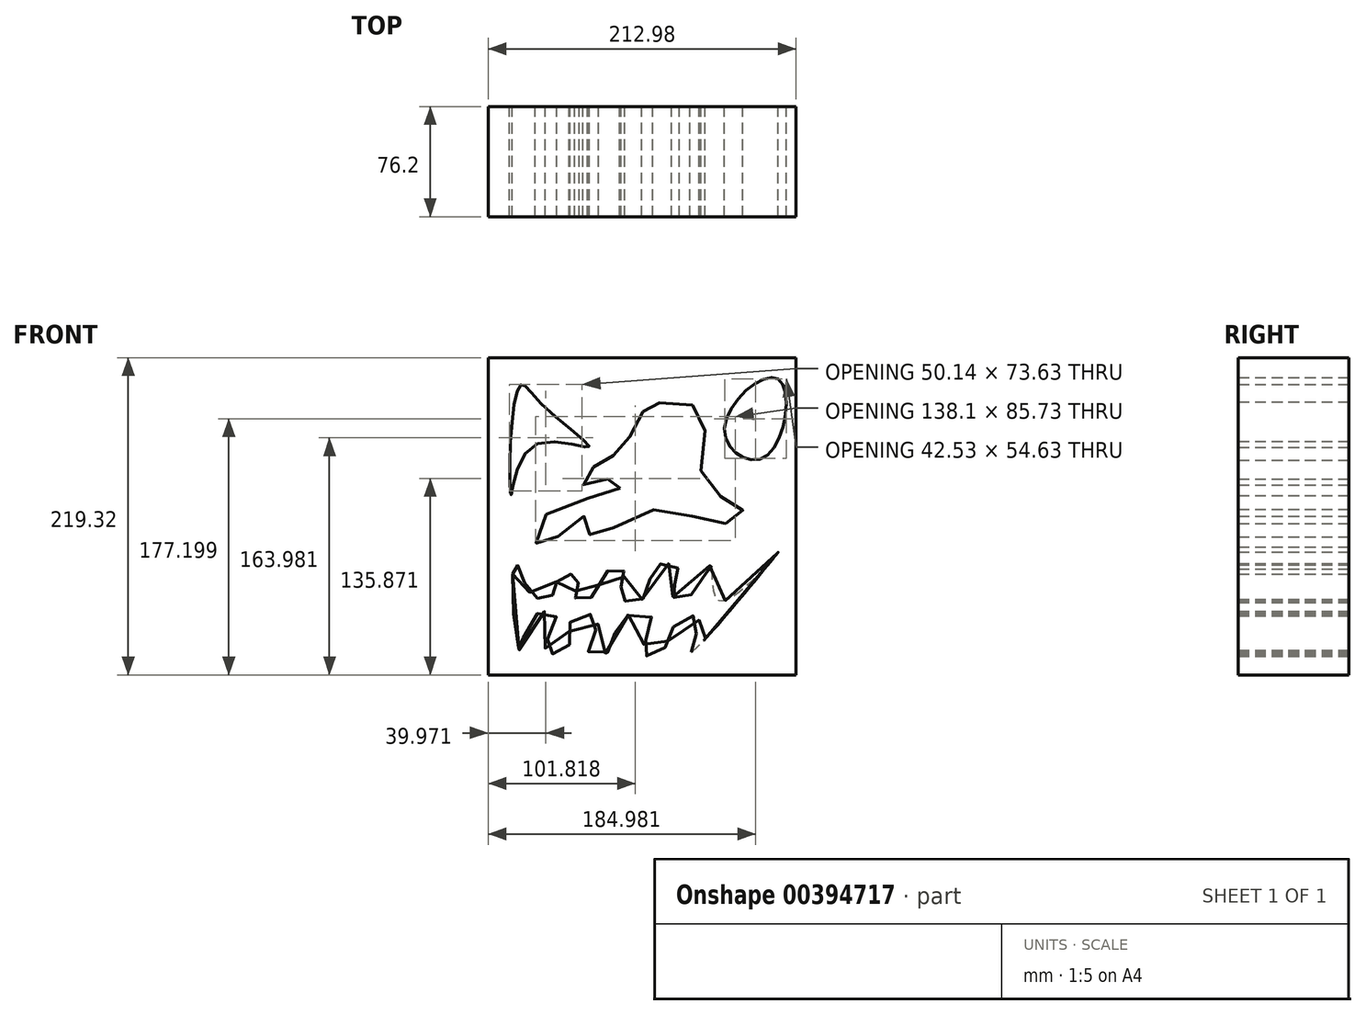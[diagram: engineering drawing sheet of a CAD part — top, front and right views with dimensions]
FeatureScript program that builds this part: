
annotation { "Feature Type Name" : "Feature", "Feature Type Description" : "" }
export const myFeature = defineFeature(function(context is Context, id is Id, definition is map)
    precondition{}
    {
        {
            var Q0;
            Q0=qCreatedBy(makeId("Front.planeOp"),FACE);
            var sketch = newSketch(context, id + "F0", { "sketchPlane" : qUnion([Q0])});
            skLineSegment(sketch, "E0.bottom", {"start": v(-106.49, 109.66) * mm, "end": v(106.49, 109.66) * mm});
            skLineSegment(sketch, "E0.top", {"start": v(-106.49, -109.66) * mm, "end": v(106.49, -109.66) * mm});
            skLineSegment(sketch, "E0.left", {"start": v(-106.49, 109.66) * mm, "end": v(-106.49, -109.66) * mm});
            skLineSegment(sketch, "E0.right", {"start": v(106.49, 109.66) * mm, "end": v(106.49, -109.66) * mm});
            skPoint(sketch, "E0.middle", {"position": v(0, 0) * mm});
            skSolve(sketch);
        }
        {
            var Q0;
            Q0 = qSketchRegion(id + "F0", true);
            extrude(context, id + "F1", {"entities" : qUnion([Q0]), "depth" : 76.2 * mm});
        }
        {
            var Q0;
            Q0=makeQuery(id+"F1.opExtrude","CAP_FACE",FACE,{"disambiguationData":[OSD([sQuery(id+"F0.wireOp",EDGE,"E0.bottom"),sQuery(id+"F0.wireOp",EDGE,"E0.top"),sQuery(id+"F0.wireOp",EDGE,"E0.left"),sQuery(id+"F0.wireOp",EDGE,"E0.right")])],"isStart":false});
            var sketch = newSketch(context, id + "F2", { "sketchPlane" : qUnion([Q0])});
            skFitSpline(sketch, "E1", {"points": [v(-69.69, 77.84) * mm, v(-83.4, 91.22) * mm, v(-90.66, 56.46) * mm, v(-90.66, 14.51) * mm, v(-74.93, 48.9) * mm, v(-36.62, 47.86) * mm, v(-69.69, 77.84) * mm]});
            skFitSpline(sketch, "E2", {"points": [v(94.05, 94.85) * mm, v(84.77, 40.96) * mm, v(56.94, 60.35) * mm, v(94.05, 94.85) * mm]});
            skFitSpline(sketch, "E3", {"points": [v(-89.45, -39.99) * mm, v(-84.61, -92.63) * mm, v(-75.34, -69.38) * mm, v(-59.2, -69.97) * mm, v(-66.87, -92.35) * mm, v(-51.54, -91.96) * mm, v(-48.72, -71.38) * mm, v(-30.57, -70.98) * mm, v(-37.43, -93.12) * mm, v(-21.3, -92.1) * mm, v(-15.65, -71.91) * mm, v(6.94, -70.64) * mm, v(0, -94.4) * mm, v(13.8, -93.26) * mm, v(23.47, -73.93) * mm, v(39.2, -71.4) * mm, v(33.55, -94) * mm, v(94.05, -24.75) * mm, v(54.12, -58.63) * mm, v(48.07, -32.95) * mm, v(33.96, -54.37) * mm, v(20.25, -53.9) * mm, v(25.49, -37.46) * mm, v(9.76, -34.33) * mm, v(0, -57.42) * mm, v(-15.24, -55.26) * mm, v(-12.42, -38.32) * mm, v(-26.54, -39.57) * mm, v(-31.78, -53.58) * mm, v(-46.3, -56.16) * mm, v(-43.88, -42.15) * mm, v(-57.6, -42.89) * mm, v(-62.03, -54.65) * mm, v(-76.14, -54.3) * mm, v(-86.22, -33.81) * mm, v(-89.45, -39.99) * mm]});
            skFitSpline(sketch, "E4", {"points": [v(-15.24, 19.35) * mm, v(-67.67, 0) * mm, v(-69.69, -21.31) * mm, v(-39.85, 0) * mm, v(-35.4, -13.5) * mm, v(6.94, 4.37) * mm, v(56.54, -5.1) * mm, v(69.45, 4.67) * mm, v(42.83, 23.2) * mm, v(41.62, 71.65) * mm, v(8.95, 77.84) * mm, v(0, 71.3) * mm, v(-15.65, 45.04) * mm, v(-29.76, 37.34) * mm, v(-40.65, 22.1) * mm, v(-19.68, 25.73) * mm, v(-15.24, 19.35) * mm]});
            skSolve(sketch);
        }
        {
            var Q0;
            Q0 = qSketchRegion(id + "F2", true);
            extrude(context, id + "F3", {"entities" : qUnion([Q0]), "operationType" : NewBodyOperationType.REMOVE, "oppositeDirection" : true, "depth" : 596.9 * mm});
        }
    });
